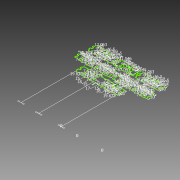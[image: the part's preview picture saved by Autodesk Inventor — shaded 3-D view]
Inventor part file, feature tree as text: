
AUTODESK INVENTOR PART (.ipt)
format: ipt  version: 2012 (Build 160160000, 160)  size: 282,624 bytes
history: native  units: mm
features: sketch x1
ambient origin geometry x8: Origin, YZ Plane, XZ Plane, XY Plane, X Axis, Y Axis, Z Axis, Center Point
feature tree (1):
  sketch  "Sketch1"  dims[d289=15.52235mm d290=2.0mm d291=15.0mm d292=15.0mm d293=15.0mm d294=15.0mm d295=15.0mm d296=15.0mm d297=15.0mm d298=7.0mm d299=30.0mm d300=121.522mm d307=7.675mm d308=7.675mm d309=11.7mm d310=6.9mm d311=23.4mm d312=11.7mm d313=6.9mm d314=7.675mm d315=7.675mm d316=7.8mm d317=7.8mm d318=38.75mm d320=7.675mm d321=7.675mm d322=11.7mm d323=6.9mm d324=23.4mm d325=11.7mm d326=6.9mm d327=7.675mm d328=7.675mm d329=7.8mm d330=7.8mm d331=38.75mm d371=33.0mm d372=33.0mm d373=0.0mm d413=12.063446mm d415=2.0mm d416=10.0mm d417=10.0mm d418=10.0mm d419=10.0mm d420=10.0mm d421=21.354415mm d422=30.0mm d423=6.0mm d424=6.0mm d425=6.0mm d429=16.5mm d430=16.5mm d431=5.9mm d432=3.0mm d433=7.8mm d434=7.8mm d435=23.4mm d436=7.675mm d437=7.675mm d438=7.675mm d439=7.675mm d440=7.8mm d441=7.8mm d442=11.7mm d443=6.9mm d444=11.7mm d445=12.063446mm d446=2.0mm d447=10.0mm d448=10.0mm d449=10.0mm d450=10.0mm d451=10.0mm d452=21.354415mm d453=30.0mm d454=6.0mm d455=6.0mm d456=6.0mm d457=16.5mm d458=16.5mm d459=5.9mm d460=3.0mm d461=7.8mm d462=7.8mm d463=23.4mm d464=7.675mm d465=7.675mm d466=7.675mm d467=7.675mm d468=7.8mm d469=7.8mm d470=11.7mm d471=6.9mm d472=11.7mm d473=11.545619mm d476=10.0mm d478=10.0mm d481=11.545619mm d482=2.0mm d483=10.0mm d484=2.0mm d485=10.0mm d486=2.0mm d487=2.0mm d488=2.0mm d489=10.0mm d490=2.0mm d491=6.0mm d492=67.091238mm d495=15.52235mm d496=2.0mm d497=15.0mm d498=15.0mm d499=15.0mm d500=15.0mm d501=15.0mm d502=15.0mm d503=15.0mm d504=7.0mm d505=30.0mm d506=121.522mm d507=7.675mm d508=7.675mm d509=11.7mm d510=6.9mm d511=23.4mm d512=11.7mm d513=6.9mm d514=7.675mm d515=7.675mm d516=7.8mm d517=7.8mm d518=38.75mm d519=7.675mm d520=7.675mm d521=11.7mm d522=6.9mm d523=23.4mm d524=11.7mm d525=6.9mm d526=7.675mm d527=7.675mm d528=7.8mm d529=7.8mm d530=38.75mm d531=33.0mm d532=33.0mm d533=0.0mm d534=2.0mm d535=16.5mm d536=16.5mm d537=5.9mm d538=3.0mm d539=7.8mm d540=7.8mm d541=7.675mm d542=7.675mm d543=7.675mm d544=7.8mm d545=7.8mm d546=11.7mm d547=6.9mm d548=11.7mm d549=7.675mm d550=7.675mm d551=11.7mm d552=6.9mm d553=23.4mm d554=11.7mm d555=6.9mm d556=7.675mm d557=7.675mm d558=15.0mm d559=15.0mm d560=15.0mm d561=15.0mm d562=18.0mm d563=18.0mm d564=30.0mm d565=6.0mm d566=6.0mm d567=17.0mm d568=19.836667mm d569=0.0mm d570=19.673333mm d571=0.0mm d572=0.0mm]
